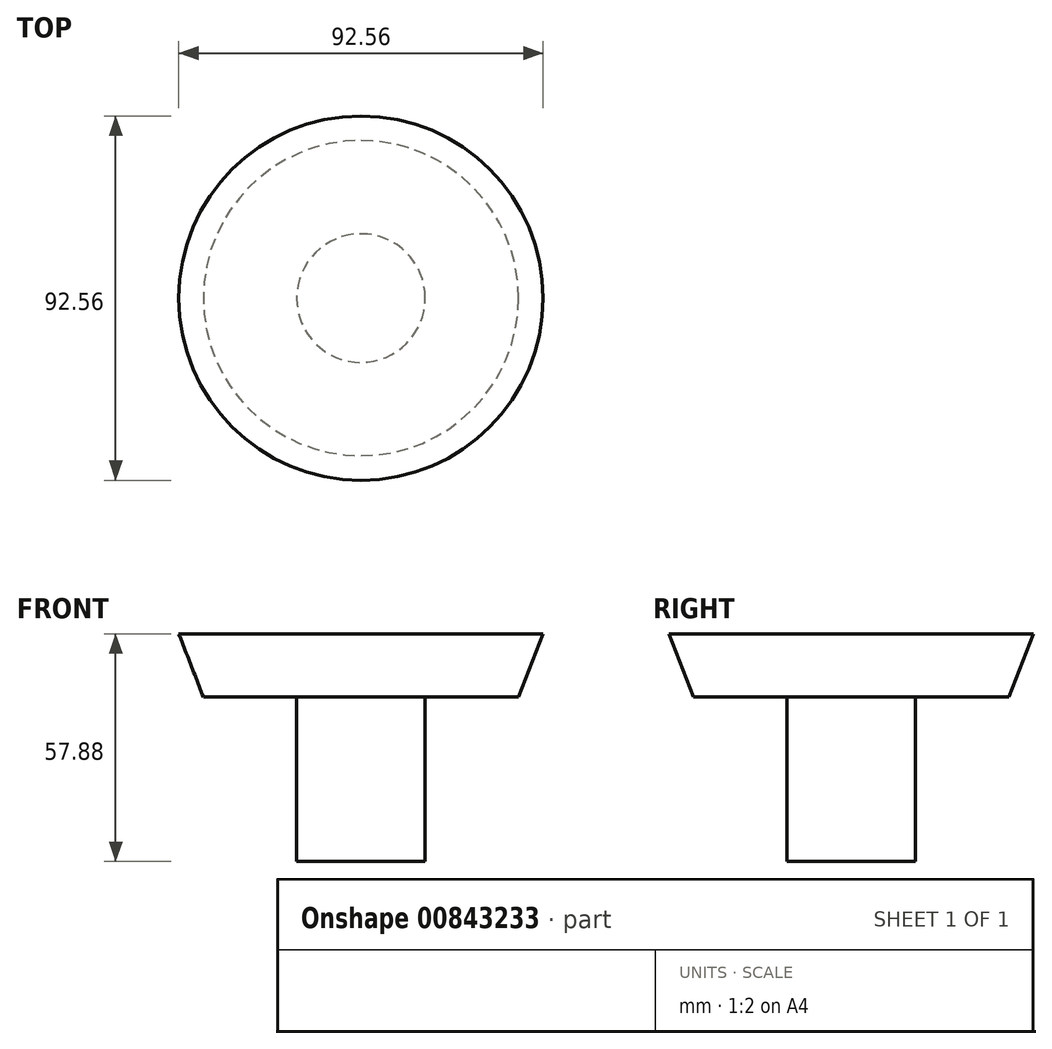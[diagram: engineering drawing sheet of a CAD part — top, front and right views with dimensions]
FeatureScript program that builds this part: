
annotation { "Feature Type Name" : "Feature", "Feature Type Description" : "" }
export const myFeature = defineFeature(function(context is Context, id is Id, definition is map)
    precondition{}
    {
        {
            var Q0;
            Q0=qCreatedBy(makeId("Front.planeOp"),FACE);
            var sketch = newSketch(context, id + "F0", { "sketchPlane" : qUnion([Q0])});
            skLineSegment(sketch, "E0", {"start": v(0, 0) * mm, "end": v(0, 57.88) * mm});
            skLineSegment(sketch, "E1", {"start": v(0, 57.88) * mm, "end": v(-40.04, 57.88) * mm});
            skLineSegment(sketch, "E2", {"start": v(-40.04, 57.88) * mm, "end": v(-40.04, 41.77) * mm});
            skLineSegment(sketch, "E3", {"start": v(-40.04, 41.77) * mm, "end": v(-16.33, 41.77) * mm});
            skLineSegment(sketch, "E4", {"start": v(-16.33, 41.77) * mm, "end": v(-16.33, 0) * mm});
            skLineSegment(sketch, "E5", {"start": v(-16.33, 0) * mm, "end": v(0, 0) * mm});
            skLineSegment(sketch, "E6", {"start": v(-40.04, 41.77) * mm, "end": v(-46.28, 57.88) * mm});
            skLineSegment(sketch, "E7", {"start": v(-46.28, 57.88) * mm, "end": v(-40.04, 57.88) * mm});
            skLineSegment(sketch, "E8", {"start": v(41.2, 62.7) * mm, "end": v(41.2, -14.35) * mm, "construction": true});
            skLineSegment(sketch, "E9.MirrorCS", {"start": v(98.74, 41.77) * mm, "end": v(98.74, 0) * mm});
            skLineSegment(sketch, "E10.MirrorCS", {"start": v(98.74, 0) * mm, "end": v(82.41, 0) * mm});
            skLineSegment(sketch, "E11.MirrorCS", {"start": v(82.41, 57.88) * mm, "end": v(122.45, 57.88) * mm});
            skLineSegment(sketch, "E12.MirrorCS", {"start": v(128.69, 57.88) * mm, "end": v(122.45, 57.88) * mm});
            skLineSegment(sketch, "E13.MirrorCS", {"start": v(122.45, 41.77) * mm, "end": v(128.69, 57.88) * mm});
            skLineSegment(sketch, "E14.MirrorCS", {"start": v(122.45, 41.77) * mm, "end": v(98.74, 41.77) * mm});
            skLineSegment(sketch, "E15.MirrorCS", {"start": v(82.41, 0) * mm, "end": v(82.41, 57.88) * mm});
            skLineSegment(sketch, "E16.MirrorCS", {"start": v(122.45, 57.88) * mm, "end": v(122.45, 41.77) * mm});
            skLineSegment(sketch, "E17.1.0.0", {"start": v(143.5, 62.7) * mm, "end": v(143.5, -14.35) * mm, "construction": true});
            skLineSegment(sketch, "E17.2.0.0", {"start": v(245.8, 62.7) * mm, "end": v(245.8, -14.35) * mm, "construction": true});
            skLineSegment(sketch, "E17.direction1", {"start": v(41.2, -14.35) * mm, "end": v(143.5, -14.35) * mm, "construction": true});
            skSolve(sketch);
        }
        {
            var Q0;
            Q0=makeQuery(id+"F0.imprint","IMPRINT",FACE,{"disambiguationData":[TD([[makeQuery(id+"F0.imprint","IMPRINT",EDGE,{"derivedFrom":sQuery(id+"F0.wireOp",EDGE,"E0")}),1.0]])]});
            var Q1;
            Q1=makeQuery(id+"F0.imprint","IMPRINT",FACE,{"disambiguationData":[TD([[makeQuery(id+"F0.imprint","IMPRINT",EDGE,{"derivedFrom":sQuery(id+"F0.wireOp",EDGE,"E2")}),-1.0]])]});
            var Q2;
            Q2=sQuery(id+"F0.wireOp",EDGE,"E0");
            revolve(context, id + "F1", {"surfaceOperationType" : NewSurfaceOperationType.NEW, "entities" : qUnion([Q0, Q1]), "axis" : qUnion([Q2]), "revolveType" : RevolveType.FULL});
        }
    });
